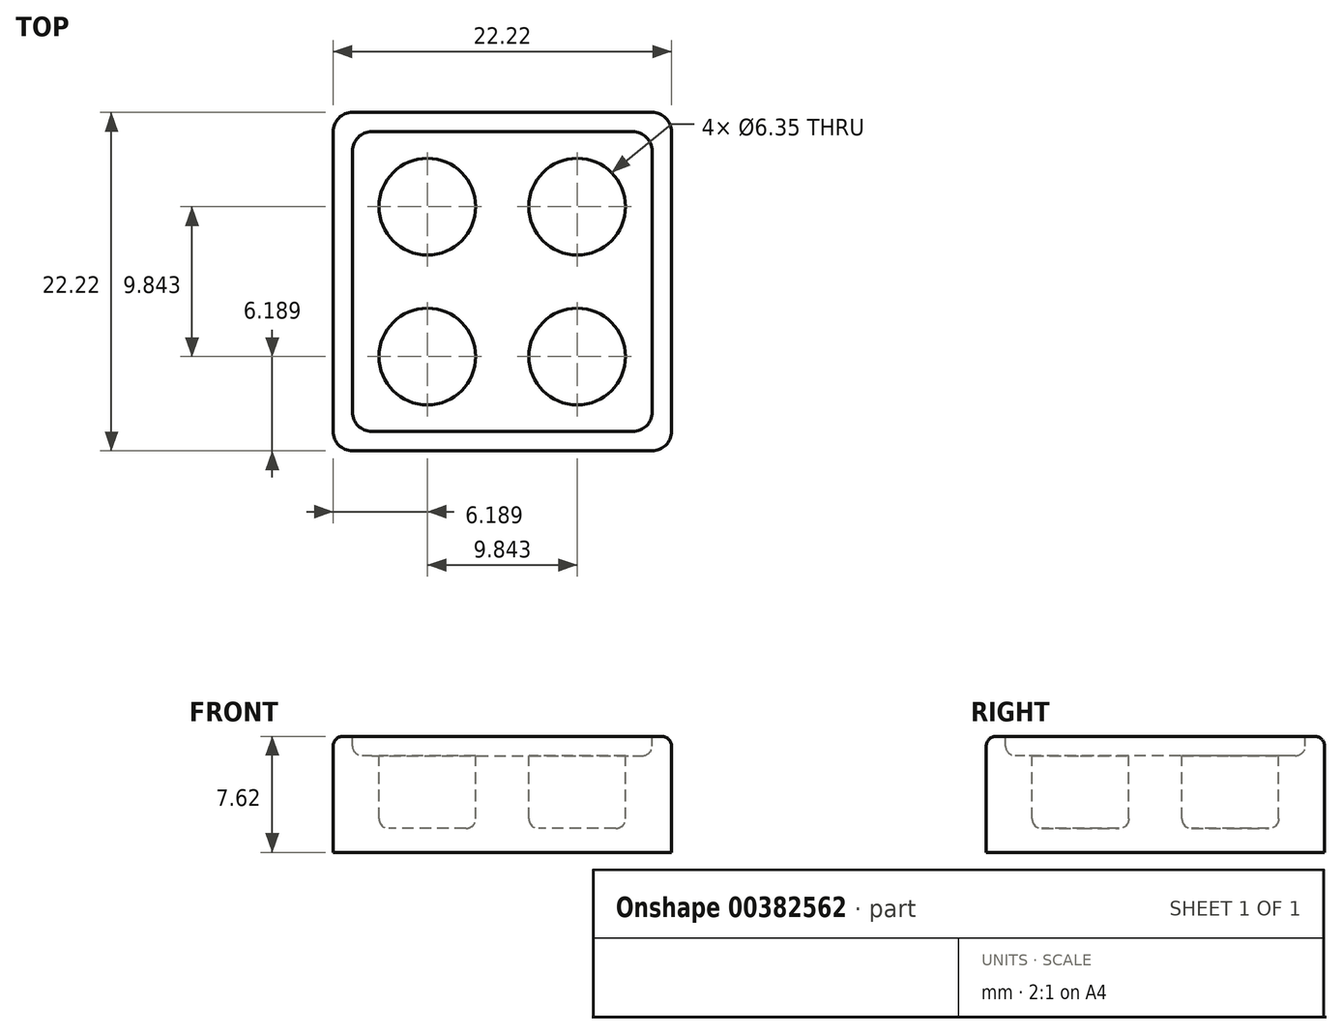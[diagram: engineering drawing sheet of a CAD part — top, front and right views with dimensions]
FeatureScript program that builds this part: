
annotation { "Feature Type Name" : "Feature", "Feature Type Description" : "" }
export const myFeature = defineFeature(function(context is Context, id is Id, definition is map)
    precondition{}
    {
        {
            var Q0;
            Q0=qCreatedBy(makeId("Top.planeOp"),FACE);
            var sketch = newSketch(context, id + "F0", { "sketchPlane" : qUnion([Q0])});
            skLineSegment(sketch, "E0.bottom", {"start": v(-9.84, 9.84) * mm, "end": v(9.84, 9.84) * mm});
            skLineSegment(sketch, "E0.top", {"start": v(-9.84, -9.84) * mm, "end": v(9.84, -9.84) * mm});
            skLineSegment(sketch, "E0.left", {"start": v(-9.84, 9.84) * mm, "end": v(-9.84, -9.84) * mm});
            skLineSegment(sketch, "E0.right", {"start": v(9.84, 9.84) * mm, "end": v(9.84, -9.84) * mm});
            skLineSegment(sketch, "E1", {"start": v(0, 9.84) * mm, "end": v(0, -9.84) * mm, "construction": true});
            skLineSegment(sketch, "E2", {"start": v(-9.84, 0) * mm, "end": v(9.84, 0) * mm, "construction": true});
            skLineSegment(sketch, "E3", {"start": v(9.84, 0) * mm, "end": v(0, 9.84) * mm, "construction": true});
            skLineSegment(sketch, "E4", {"start": v(0, 9.84) * mm, "end": v(-9.84, 0) * mm, "construction": true});
            skLineSegment(sketch, "E5", {"start": v(-9.84, 0) * mm, "end": v(0, -9.84) * mm, "construction": true});
            skLineSegment(sketch, "E6", {"start": v(0, -9.84) * mm, "end": v(9.84, 0) * mm, "construction": true});
            skCircle(sketch, "E7", {"center": v(-4.92, 4.92) * mm, "radius": 3.18 * mm});
            skCircle(sketch, "E8", {"center": v(-4.92, -4.92) * mm, "radius": 3.18 * mm});
            skCircle(sketch, "E9", {"center": v(4.92, 4.92) * mm, "radius": 3.18 * mm});
            skCircle(sketch, "E10", {"center": v(4.92, -4.92) * mm, "radius": 3.18 * mm});
            skLineSegment(sketch, "E11", {"start": v(4.92, -4.92) * mm, "end": v(4.92, -9.84) * mm, "construction": true});
            skLineSegment(sketch, "E12", {"start": v(-4.92, -4.92) * mm, "end": v(-4.92, -9.84) * mm, "construction": true});
            skLineSegment(sketch, "E13", {"start": v(-9.84, -9.84) * mm, "end": v(-11.11, -11.11) * mm});
            skLineSegment(sketch, "E14", {"start": v(-11.11, -11.11) * mm, "end": v(11.11, -11.11) * mm});
            skLineSegment(sketch, "E15", {"start": v(11.11, -11.11) * mm, "end": v(9.84, -9.84) * mm});
            skLineSegment(sketch, "E16", {"start": v(11.11, -11.11) * mm, "end": v(11.11, 11.11) * mm});
            skLineSegment(sketch, "E17", {"start": v(11.11, 11.11) * mm, "end": v(9.84, 9.84) * mm});
            skLineSegment(sketch, "E18", {"start": v(11.11, 11.11) * mm, "end": v(-11.11, 11.11) * mm});
            skLineSegment(sketch, "E19", {"start": v(-11.11, 11.11) * mm, "end": v(-9.84, 9.84) * mm});
            skLineSegment(sketch, "E20", {"start": v(-11.11, 11.11) * mm, "end": v(-11.11, -11.11) * mm});
            skSolve(sketch);
        }
        {
            var Q0;
            Q0=makeQuery(id+"F0.imprint","IMPRINT",FACE,{"disambiguationData":[TD([[makeQuery(id+"F0.imprint","IMPRINT",EDGE,{"derivedFrom":sQuery(id+"F0.wireOp",EDGE,"E0.bottom")}),1.0]])]});
            var Q1;
            Q1=makeQuery(id+"F0.imprint","IMPRINT",FACE,{"disambiguationData":[TD([[makeQuery(id+"F0.imprint","IMPRINT",EDGE,{"derivedFrom":sQuery(id+"F0.wireOp",EDGE,"E0.right")}),1.0]])]});
            var Q2;
            Q2=makeQuery(id+"F0.imprint","IMPRINT",FACE,{"disambiguationData":[TD([[makeQuery(id+"F0.imprint","IMPRINT",EDGE,{"derivedFrom":sQuery(id+"F0.wireOp",EDGE,"E0.left")}),-1.0]])]});
            var Q3;
            Q3=makeQuery(id+"F0.imprint","IMPRINT",FACE,{"disambiguationData":[TD([[makeQuery(id+"F0.imprint","IMPRINT",EDGE,{"derivedFrom":sQuery(id+"F0.wireOp",EDGE,"E0.top")}),-1.0]])]});
            var Q4;
            Q4=makeQuery(id+"F0.imprint","IMPRINT",FACE,{"disambiguationData":[TD([[makeQuery(id+"F0.imprint","IMPRINT",EDGE,{"derivedFrom":sQuery(id+"F0.wireOp",EDGE,"E0.bottom")}),-1.0]])]});
            var Q5;
            Q5=makeQuery(id+"F0.imprint","IMPRINT",FACE,{"disambiguationData":[TD([[makeQuery(id+"F0.imprint","IMPRINT",EDGE,{"derivedFrom":sQuery(id+"F0.wireOp",EDGE,"E7")}),1.0]])]});
            var Q6;
            Q6=makeQuery(id+"F0.imprint","IMPRINT",FACE,{"disambiguationData":[TD([[makeQuery(id+"F0.imprint","IMPRINT",EDGE,{"derivedFrom":sQuery(id+"F0.wireOp",EDGE,"E9")}),1.0]])]});
            var Q7;
            Q7=makeQuery(id+"F0.imprint","IMPRINT",FACE,{"disambiguationData":[TD([[makeQuery(id+"F0.imprint","IMPRINT",EDGE,{"derivedFrom":sQuery(id+"F0.wireOp",EDGE,"E8")}),1.0]])]});
            var Q8;
            Q8=makeQuery(id+"F0.imprint","IMPRINT",FACE,{"disambiguationData":[TD([[makeQuery(id+"F0.imprint","IMPRINT",EDGE,{"derivedFrom":sQuery(id+"F0.wireOp",EDGE,"E10")}),1.0]])]});
            extrude(context, id + "F1", {"entities" : qUnion([Q0, Q1, Q2, Q3, Q4, Q5, Q6, Q7, Q8]), "oppositeDirection" : true, "depth" : 7.62 * mm, "offsetDistance" : 25.4 * mm});
        }
        {
            var Q0;
            Q0=makeQuery(id+"F0.imprint","IMPRINT",FACE,{"disambiguationData":[TD([[makeQuery(id+"F0.imprint","IMPRINT",EDGE,{"derivedFrom":sQuery(id+"F0.wireOp",EDGE,"E0.bottom")}),-1.0]])]});
            var Q1;
            Q1=makeQuery(id+"F0.imprint","IMPRINT",FACE,{"disambiguationData":[TD([[makeQuery(id+"F0.imprint","IMPRINT",EDGE,{"derivedFrom":sQuery(id+"F0.wireOp",EDGE,"E7")}),1.0]])]});
            var Q2;
            Q2=makeQuery(id+"F0.imprint","IMPRINT",FACE,{"disambiguationData":[TD([[makeQuery(id+"F0.imprint","IMPRINT",EDGE,{"derivedFrom":sQuery(id+"F0.wireOp",EDGE,"E9")}),1.0]])]});
            var Q3;
            Q3=makeQuery(id+"F0.imprint","IMPRINT",FACE,{"disambiguationData":[TD([[makeQuery(id+"F0.imprint","IMPRINT",EDGE,{"derivedFrom":sQuery(id+"F0.wireOp",EDGE,"E10")}),1.0]])]});
            var Q4;
            Q4=makeQuery(id+"F0.imprint","IMPRINT",FACE,{"disambiguationData":[TD([[makeQuery(id+"F0.imprint","IMPRINT",EDGE,{"derivedFrom":sQuery(id+"F0.wireOp",EDGE,"E8")}),1.0]])]});
            extrude(context, id + "F2", {"entities" : qUnion([Q0, Q1, Q2, Q3, Q4]), "operationType" : NewBodyOperationType.REMOVE, "oppositeDirection" : true, "depth" : 1.27 * mm, "offsetDistance" : 25.4 * mm});
        }
        {
            var Q0;
            Q0=makeQuery(id+"F0.imprint","IMPRINT",FACE,{"disambiguationData":[TD([[makeQuery(id+"F0.imprint","IMPRINT",EDGE,{"derivedFrom":sQuery(id+"F0.wireOp",EDGE,"E7")}),1.0]])]});
            var Q1;
            Q1=makeQuery(id+"F0.imprint","IMPRINT",FACE,{"disambiguationData":[TD([[makeQuery(id+"F0.imprint","IMPRINT",EDGE,{"derivedFrom":sQuery(id+"F0.wireOp",EDGE,"E8")}),1.0]])]});
            var Q2;
            Q2=makeQuery(id+"F0.imprint","IMPRINT",FACE,{"disambiguationData":[TD([[makeQuery(id+"F0.imprint","IMPRINT",EDGE,{"derivedFrom":sQuery(id+"F0.wireOp",EDGE,"E10")}),1.0]])]});
            var Q3;
            Q3=makeQuery(id+"F0.imprint","IMPRINT",FACE,{"disambiguationData":[TD([[makeQuery(id+"F0.imprint","IMPRINT",EDGE,{"derivedFrom":sQuery(id+"F0.wireOp",EDGE,"E9")}),1.0]])]});
            extrude(context, id + "F3", {"entities" : qUnion([Q0, Q1, Q2, Q3]), "operationType" : NewBodyOperationType.REMOVE, "oppositeDirection" : true, "depth" : 6.05 * mm, "offsetDistance" : 25.4 * mm});
        }
        {
            var Q0;
            Q0=makeQuery(id+"F1.opExtrude","SWEPT_EDGE",EDGE,{"disambiguationData":[OSD([sQuery(id+"F0.wireOp",EDGE,"E14"),sQuery(id+"F0.wireOp",EDGE,"E15"),sQuery(id+"F0.wireOp",EDGE,"E16")])]});
            var Q1;
            Q1=makeQuery(id+"F1.opExtrude","SWEPT_EDGE",EDGE,{"disambiguationData":[OSD([sQuery(id+"F0.wireOp",EDGE,"E16"),sQuery(id+"F0.wireOp",EDGE,"E17"),sQuery(id+"F0.wireOp",EDGE,"E18")])]});
            var Q2;
            Q2=makeQuery(id+"F1.opExtrude","SWEPT_EDGE",EDGE,{"disambiguationData":[OSD([sQuery(id+"F0.wireOp",EDGE,"E13"),sQuery(id+"F0.wireOp",EDGE,"E14"),sQuery(id+"F0.wireOp",EDGE,"E20")])]});
            var Q3;
            Q3=makeQuery(id+"F1.opExtrude","SWEPT_EDGE",EDGE,{"disambiguationData":[OSD([sQuery(id+"F0.wireOp",EDGE,"E18"),sQuery(id+"F0.wireOp",EDGE,"E19"),sQuery(id+"F0.wireOp",EDGE,"E20")])]});
            var Q4;
            Q4=makeQuery(id+"F2.boolean.opBoolean","COPY",EDGE,{"derivedFrom":makeQuery(id+"F2.opExtrude","SWEPT_EDGE",EDGE,{"disambiguationData":[OSD([sQuery(id+"F0.wireOp",EDGE,"E0.top"),sQuery(id+"F0.wireOp",EDGE,"E0.left"),sQuery(id+"F0.wireOp",EDGE,"E13")])]})});
            var Q5;
            Q5=makeQuery(id+"F2.boolean.opBoolean","COPY",EDGE,{"derivedFrom":makeQuery(id+"F2.opExtrude","SWEPT_EDGE",EDGE,{"disambiguationData":[OSD([sQuery(id+"F0.wireOp",EDGE,"E0.bottom"),sQuery(id+"F0.wireOp",EDGE,"E0.left"),sQuery(id+"F0.wireOp",EDGE,"E19")])]})});
            var Q6;
            Q6=makeQuery(id+"F2.boolean.opBoolean","COPY",EDGE,{"derivedFrom":makeQuery(id+"F2.opExtrude","SWEPT_EDGE",EDGE,{"disambiguationData":[OSD([sQuery(id+"F0.wireOp",EDGE,"E0.bottom"),sQuery(id+"F0.wireOp",EDGE,"E0.right"),sQuery(id+"F0.wireOp",EDGE,"E17")])]})});
            var Q7;
            Q7=makeQuery(id+"F2.boolean.opBoolean","COPY",EDGE,{"derivedFrom":makeQuery(id+"F2.opExtrude","SWEPT_EDGE",EDGE,{"disambiguationData":[OSD([sQuery(id+"F0.wireOp",EDGE,"E0.top"),sQuery(id+"F0.wireOp",EDGE,"E0.right"),sQuery(id+"F0.wireOp",EDGE,"E15")])]})});
            fillet(context, id + "F4", {"entities" : qUnion([Q0, Q1, Q2, Q3, Q4, Q5, Q6, Q7]), "radius" : 1.27 * mm, "tangentPropagation" : true, "allowEdgeOverflow" : false});
        }
        {
            var Q0;
            Q0=makeQuery(id+"F3.boolean.opBoolean","COPY",EDGE,{"derivedFrom":makeQuery(id+"F3.opExtrude","CAP_EDGE",EDGE,{"disambiguationData":[OSD([sQuery(id+"F0.wireOp",EDGE,"E7")])],"isStart":false})});
            var Q1;
            Q1=makeQuery(id+"F3.boolean.opBoolean","COPY",EDGE,{"derivedFrom":makeQuery(id+"F3.opExtrude","CAP_EDGE",EDGE,{"disambiguationData":[OSD([sQuery(id+"F0.wireOp",EDGE,"E9")])],"isStart":false})});
            var Q2;
            Q2=makeQuery(id+"F3.boolean.opBoolean","COPY",EDGE,{"derivedFrom":makeQuery(id+"F3.opExtrude","CAP_EDGE",EDGE,{"disambiguationData":[OSD([sQuery(id+"F0.wireOp",EDGE,"E10")])],"isStart":false})});
            var Q3;
            Q3=makeQuery(id+"F3.boolean.opBoolean","COPY",EDGE,{"derivedFrom":makeQuery(id+"F3.opExtrude","CAP_EDGE",EDGE,{"disambiguationData":[OSD([sQuery(id+"F0.wireOp",EDGE,"E8")])],"isStart":false})});
            var Q4;
            Q4=makeQuery(id+"F2.boolean.opBoolean","COPY",EDGE,{"derivedFrom":makeQuery(id+"F2.opExtrude","CAP_EDGE",EDGE,{"disambiguationData":[OSD([sQuery(id+"F0.wireOp",EDGE,"E0.left")])],"isStart":false})});
            var Q5;
            Q5=makeQuery(id+"F2.boolean.opBoolean","COPY",EDGE,{"derivedFrom":makeQuery(id+"F2.opExtrude","CAP_EDGE",EDGE,{"disambiguationData":[OSD([sQuery(id+"F0.wireOp",EDGE,"E0.bottom")])],"isStart":true})});
            var Q6;
            Q6=makeQuery(id+"F1.opExtrude","CAP_EDGE",EDGE,{"disambiguationData":[OSD([sQuery(id+"F0.wireOp",EDGE,"E20")])],"isStart":true});
            fillet(context, id + "F5", {"entities" : qUnion([Q0, Q1, Q2, Q3, Q4, Q5, Q6]), "radius" : 0.64 * mm, "tangentPropagation" : true, "allowEdgeOverflow" : false});
        }
    });
